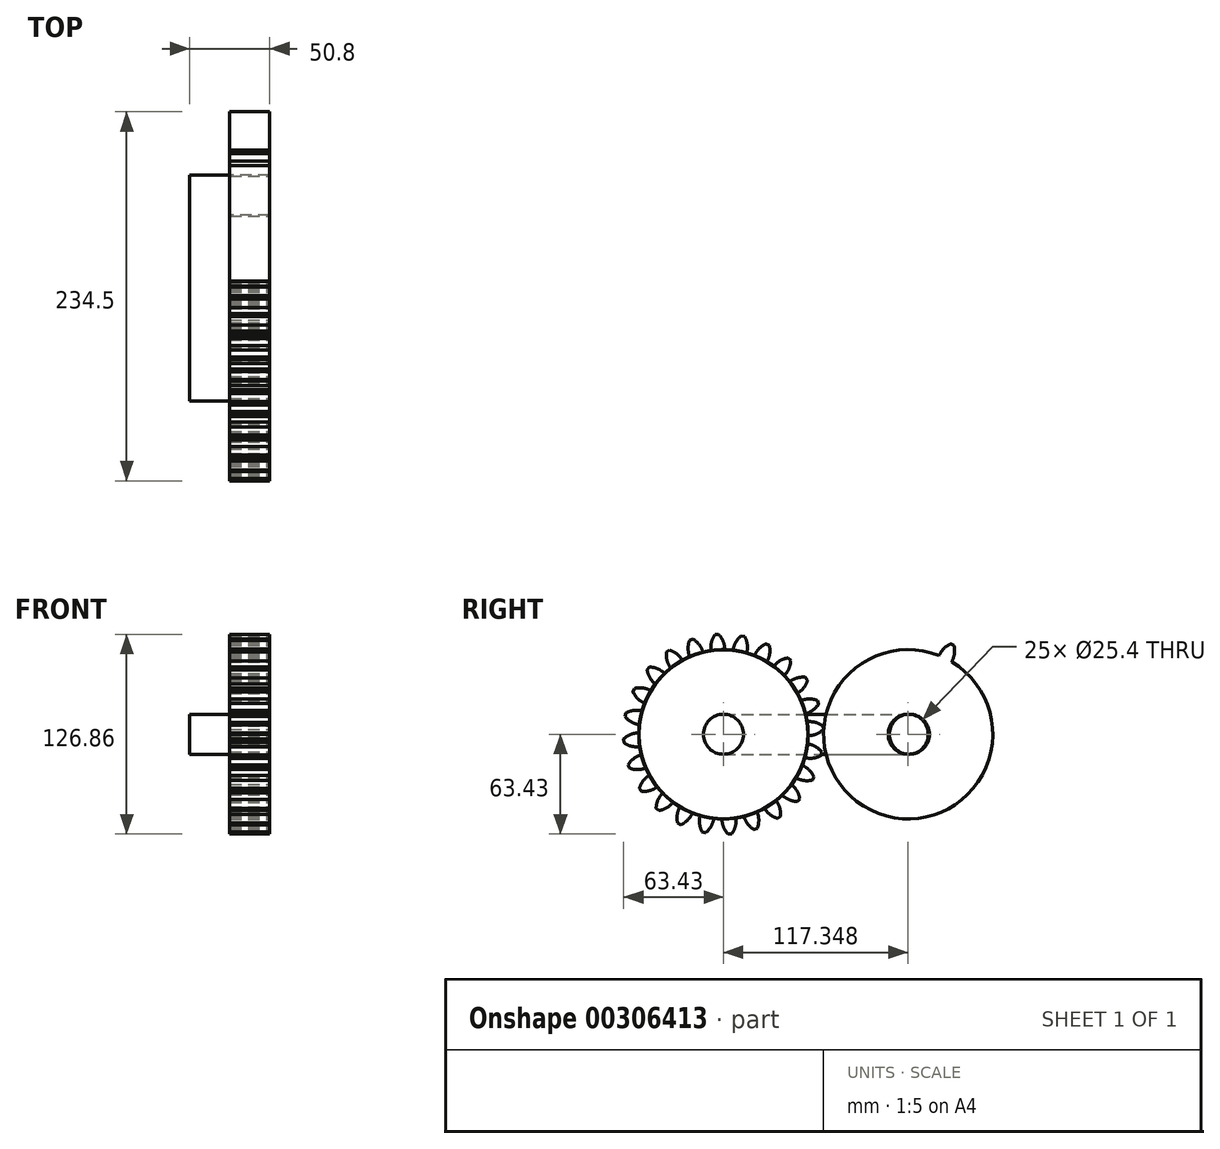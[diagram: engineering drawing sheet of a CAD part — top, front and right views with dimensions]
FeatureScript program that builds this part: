
annotation { "Feature Type Name" : "Feature", "Feature Type Description" : "" }
export const myFeature = defineFeature(function(context is Context, id is Id, definition is map)
    precondition{}
    {
        {
            var Q0;
            Q0=qCreatedBy(makeId("Right.planeOp"),FACE);
            var sketch = newSketch(context, id + "F0", { "sketchPlane" : qUnion([Q0])});
            skLineSegment(sketch, "E0.bottom", {"start": v(0, 0) * mm, "end": v(118.11, 0) * mm});
            skLineSegment(sketch, "E0.top", {"start": v(0, 25.4) * mm, "end": v(118.11, 25.4) * mm});
            skLineSegment(sketch, "E0.left", {"start": v(0, 0) * mm, "end": v(0, 25.4) * mm});
            skLineSegment(sketch, "E0.right", {"start": v(118.11, 0) * mm, "end": v(118.11, 25.4) * mm});
            skCircle(sketch, "E1", {"center": v(0, 12.7) * mm, "radius": 12.7 * mm});
            skCircle(sketch, "E2", {"center": v(118.11, 12.7) * mm, "radius": 12.7 * mm});
            skSolve(sketch);
        }
        {
            var Q0;
            Q0 = qSketchRegion(id + "F0", true);
            extrude(context, id + "F1", {"entities" : qUnion([Q0]), "depth" : 25.4 * mm});
        }
        {
            var Q0;
            {var subQ0=sQuery(id+"F0.wireOp",EDGE,"E0.right");Q0=makeQuery(id+"F0.imprint","IMPRINT",FACE,{"disambiguationData":[TD([[makeQuery(id+"F0.imprint","IMPRINT",EDGE,{"derivedFrom":subQ0}),-1.0]])]});}
            var Q1;
            {var subQ0=sQuery(id+"F0.wireOp",EDGE,"E0.right");Q1=makeQuery(id+"F0.imprint","IMPRINT",FACE,{"disambiguationData":[TD([[makeQuery(id+"F0.imprint","IMPRINT",EDGE,{"derivedFrom":subQ0}),1.0]])]});}
            extrude(context, id + "F2", {"entities" : qUnion([Q0, Q1]), "operationType" : NewBodyOperationType.ADD, "depth" : 50.8 * mm});
        }
        {
            var Q0;
            {var subQ0=sQuery(id+"F0.wireOp",EDGE,"E0.left");Q0=makeQuery(id+"F0.imprint","IMPRINT",FACE,{"disambiguationData":[TD([[makeQuery(id+"F0.imprint","IMPRINT",EDGE,{"derivedFrom":subQ0}),-1.0]])]});}
            var Q1;
            {var subQ0=sQuery(id+"F0.wireOp",EDGE,"E0.left");Q1=makeQuery(id+"F0.imprint","IMPRINT",FACE,{"disambiguationData":[TD([[makeQuery(id+"F0.imprint","IMPRINT",EDGE,{"derivedFrom":subQ0}),1.0]])]});}
            extrude(context, id + "F3", {"entities" : qUnion([Q0, Q1]), "operationType" : NewBodyOperationType.ADD, "depth" : 50.8 * mm});
        }
        {
            var Q0;
            Q0=makeQuery(id+"F3.opExtrude","CAP_FACE",FACE,{"disambiguationData":[OSD([sQuery(id+"F0.wireOp",EDGE,"E1")])],"isStart":false});
            var sketch = newSketch(context, id + "F4", { "sketchPlane" : qUnion([Q0])});
            skCircle(sketch, "E3", {"center": v(0, 12.7) * mm, "radius": 12.7 * mm});
            skCircle(sketch, "E4", {"center": v(0, 12.7) * mm, "radius": 53.72 * mm});
            skCircle(sketch, "E5", {"center": v(0, 12.7) * mm, "radius": 58.67 * mm, "construction": true});
            skCircle(sketch, "E6", {"center": v(0, 12.7) * mm, "radius": 63.5 * mm, "construction": true});
            skLineSegment(sketch, "E7", {"start": v(0, 12.7) * mm, "end": v(0, 88.86) * mm, "construction": true});
            skLineSegment(sketch, "E8", {"start": v(0, 12.7) * mm, "end": v(-5.23, 92.54) * mm, "construction": true});
            skLineSegment(sketch, "E9", {"start": v(0, 71.37) * mm, "end": v(-55.97, 71.37) * mm, "construction": true});
            skLineSegment(sketch, "E10", {"start": v(0, 71.37) * mm, "end": v(-55.38, 51.22) * mm, "construction": true});
            skCircle(sketch, "E11", {"center": v(0, 12.7) * mm, "radius": 55.14 * mm, "construction": true});
            skCircle(sketch, "E12", {"center": v(0, 71.37) * mm, "radius": 14.6 * mm, "construction": true});
            skCircle(sketch, "E13", {"center": v(-13.63, 66.12) * mm, "radius": 14.6 * mm, "construction": true});
            skArc(sketch, "E14", {"start": v(0, 71.37) * mm, "mid": v(-1.27, 73.9) * mm, "end": v(-2.99, 76.13) * mm});
            skArc(sketch, "E15", {"start": v(0.97, 66.41) * mm, "mid": v(0.67, 68.93) * mm, "end": v(0, 71.37) * mm});
            skArc(sketch, "E16.MirrorCS", {"start": v(-7.66, 70.87) * mm, "mid": v(-6.73, 73.54) * mm, "end": v(-5.32, 75.98) * mm});
            skLineSegment(sketch, "E17", {"start": v(-5.32, 75.98) * mm, "end": v(-2.99, 76.13) * mm});
            skArc(sketch, "E18.MirrorCS", {"start": v(-7.98, 65.83) * mm, "mid": v(-8, 68.36) * mm, "end": v(-7.66, 70.87) * mm});
            skSolve(sketch);
        }
        {
            var Q0;
            Q0 = qSketchRegion(id + "F4", true);
            extrude(context, id + "F5", {"entities" : qUnion([Q0]), "oppositeDirection" : true, "depth" : 25.4 * mm});
        }
        {
            var Q0;
            Q0=makeQuery(id+"F5.opExtrude","SWEPT_BODY",BODY,{"disambiguationData":[OSD([sQuery(id+"F4.wireOp",EDGE,"E3"),sQuery(id+"F4.wireOp",EDGE,"E4"),sQuery(id+"F4.wireOp",EDGE,"E14"),sQuery(id+"F4.wireOp",EDGE,"E15"),sQuery(id+"F4.wireOp",EDGE,"E16.MirrorCS"),sQuery(id+"F4.wireOp",EDGE,"E17"),sQuery(id+"F4.wireOp",EDGE,"E18.MirrorCS")])]});
            var Q1;
            Q1=makeQuery(id+"F5.opExtrude","SWEPT_FACE",FACE,{"disambiguationData":[OSD([sQuery(id+"F4.wireOp",EDGE,"E4")])]});
            circularPattern(context, id + "F6", {"entities" : qUnion([Q0]), "axis" : qUnion([Q1]), "angle" : 15 * degree, "instanceCount" : 24});
        }
        {
            var Q0;
            Q0=makeQuery(id+"F6.opPattern","COPY",BODY,{"derivedFrom":makeQuery(id+"F5.opExtrude","SWEPT_BODY",BODY,{"disambiguationData":[OSD([sQuery(id+"F4.wireOp",EDGE,"E3"),sQuery(id+"F4.wireOp",EDGE,"E4"),sQuery(id+"F4.wireOp",EDGE,"E14"),sQuery(id+"F4.wireOp",EDGE,"E15"),sQuery(id+"F4.wireOp",EDGE,"E16.MirrorCS"),sQuery(id+"F4.wireOp",EDGE,"E17"),sQuery(id+"F4.wireOp",EDGE,"E18.MirrorCS")])]}),"instanceName":"22"});
            transform(context, id + "F7", {"entities" : qUnion([Q0]), "transformType" : TransformType.TRANSLATION_3D, "dx" : 0 * mm, "dy" : 117.35 * mm, "dz" : 0 * mm, "makeCopy" : true});
        }
    });
